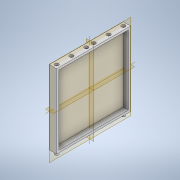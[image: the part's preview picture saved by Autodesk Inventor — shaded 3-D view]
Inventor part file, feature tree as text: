
AUTODESK INVENTOR PART (.ipt)
format: ipt  version: 2022.4 (Build 264492010, 492A)  size: 158,720 bytes
history: native  units: mm
features: extrude x4, sketch x4
ambient origin geometry x8: Origin, YZ Plane, XZ Plane, XY Plane, X Axis, Y Axis, Z Axis, Center Point
bodies: Solid1 (feature_tree)
feature tree (8):
  extrude  "Extrusion1"  Depth=99.75mm
  extrude  "Extrusion2"  Depth=93.75mm
  extrude  "Extrusion3"  Depth=7.0mm TaperAngle=0.0deg
  extrude  "Extrusion4"  Depth=4.875mm
  sketch  "Sketch2"  dims[d0=99.75mm d1=99.75mm]
  sketch  "Sketch3"  dims[d2=9.75mm d3=0.0mm d4=93.75mm]
  sketch  "Sketch5"  dims[d5=93.75mm d6=7.0mm d7=0.0mm]
  sketch  "Sketch6"  dims[d26=5.0mm d27=4.875mm d28=30.0mm d30=20.0mm d31=10.0mm d33=10.0mm d35=5.0mm d36=4.875mm d37=30.0mm d39=20.0mm d40=10.0mm d42=10.0mm d44=7.0mm d45=0.0mm d46=4.75mm d47=4.875mm d64=4.75mm d65=0.0mm]
